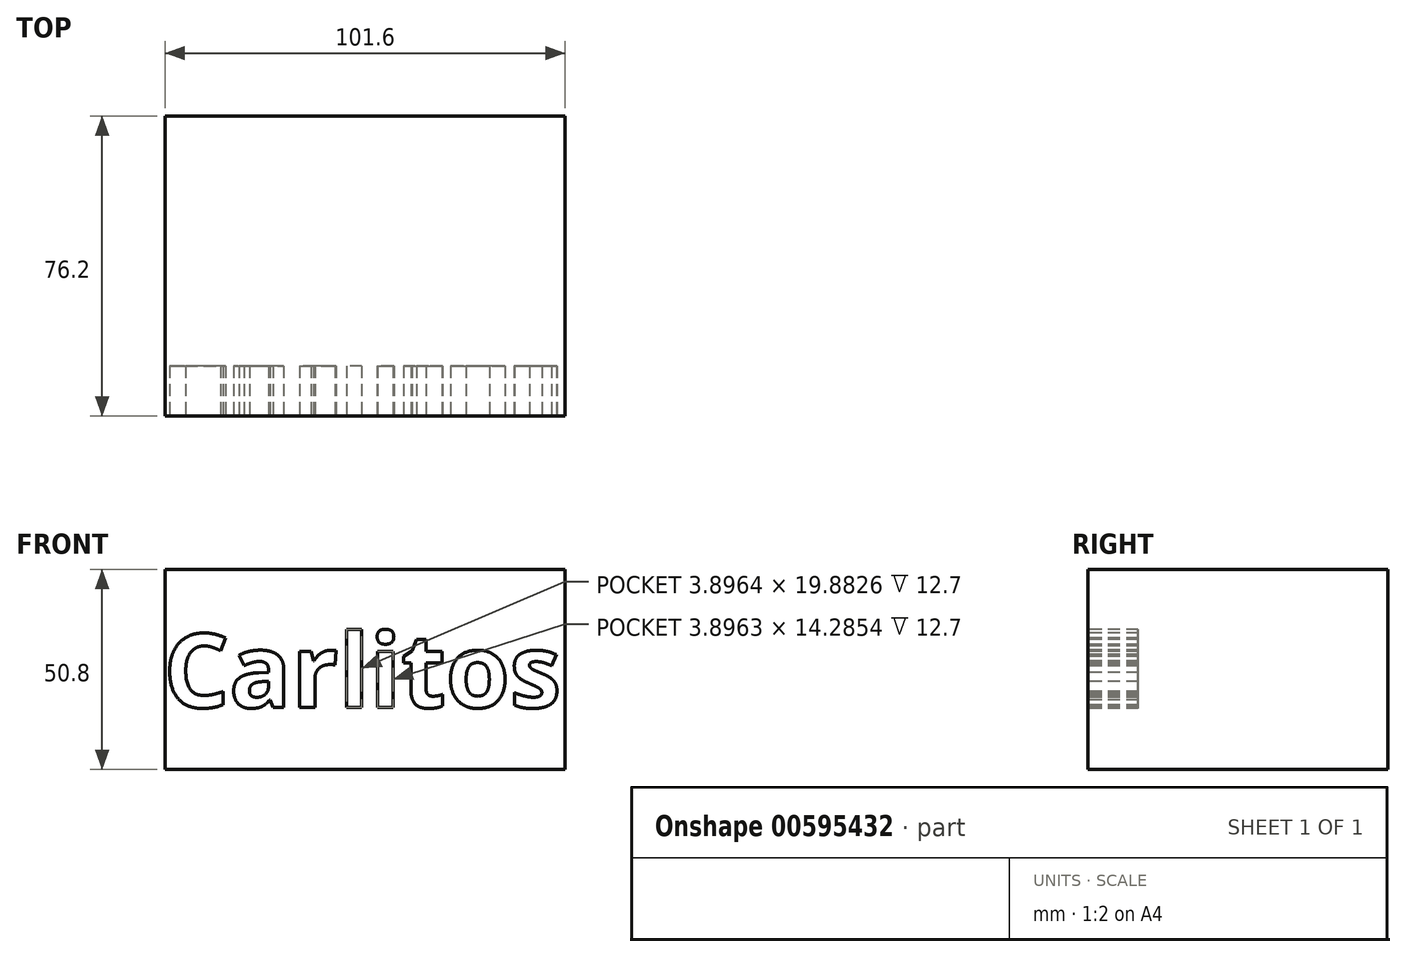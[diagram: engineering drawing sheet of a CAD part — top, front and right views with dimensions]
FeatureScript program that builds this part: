
annotation { "Feature Type Name" : "Feature", "Feature Type Description" : "" }
export const myFeature = defineFeature(function(context is Context, id is Id, definition is map)
    precondition{}
    {
        {
            var Q0;
            Q0=qCreatedBy(makeId("Right.planeOp"),FACE);
            var sketch = newSketch(context, id + "F0", { "sketchPlane" : qUnion([Q0])});
            skLineSegment(sketch, "E0.bottom", {"start": v(-125.49, -66.3) * mm, "end": v(-49.29, -66.3) * mm});
            skLineSegment(sketch, "E0.top", {"start": v(-125.49, -117.1) * mm, "end": v(-49.29, -117.1) * mm});
            skLineSegment(sketch, "E0.left", {"start": v(-125.49, -66.3) * mm, "end": v(-125.49, -117.1) * mm});
            skLineSegment(sketch, "E0.right", {"start": v(-49.29, -66.3) * mm, "end": v(-49.29, -117.1) * mm});
            skSolve(sketch);
        }
        {
            var Q0;
            Q0=makeQuery(id+"F0.imprint","IMPRINT",FACE,{"disambiguationData":[TD([[makeQuery(id+"F0.imprint","IMPRINT",EDGE,{"derivedFrom":sQuery(id+"F0.wireOp",EDGE,"E0.bottom")}),-1.0]])]});
            extrude(context, id + "F1", {"entities" : qUnion([Q0]), "depth" : 101.6 * mm, "offsetDistance" : 25.4 * mm});
        }
        {
            var Q0;
            Q0=makeQuery(id+"F1.opExtrude","SWEPT_FACE",FACE,{"disambiguationData":[OSD([sQuery(id+"F0.wireOp",EDGE,"E0.left")])]});
            var sketch = newSketch(context, id + "F2", { "sketchPlane" : qUnion([Q0])});
            skText(sketch, "E1", { "text": "Carlitos", "fontName": "OpenSans-Bold.ttf"});
            const initialGuessF2  = {"E1": [-0.00034, -0.10136, 1, 0, 0.01884]};
            skSetInitialGuess(sketch, initialGuessF2);
            skSolve(sketch);
        }
        {
            var Q0;
            Q0 = qSketchRegion(id + "F2", true);
            extrude(context, id + "F3", {"entities" : qUnion([Q0]), "operationType" : NewBodyOperationType.REMOVE, "oppositeDirection" : true, "depth" : 12.7 * mm, "offsetDistance" : 25.4 * mm});
        }
    });
